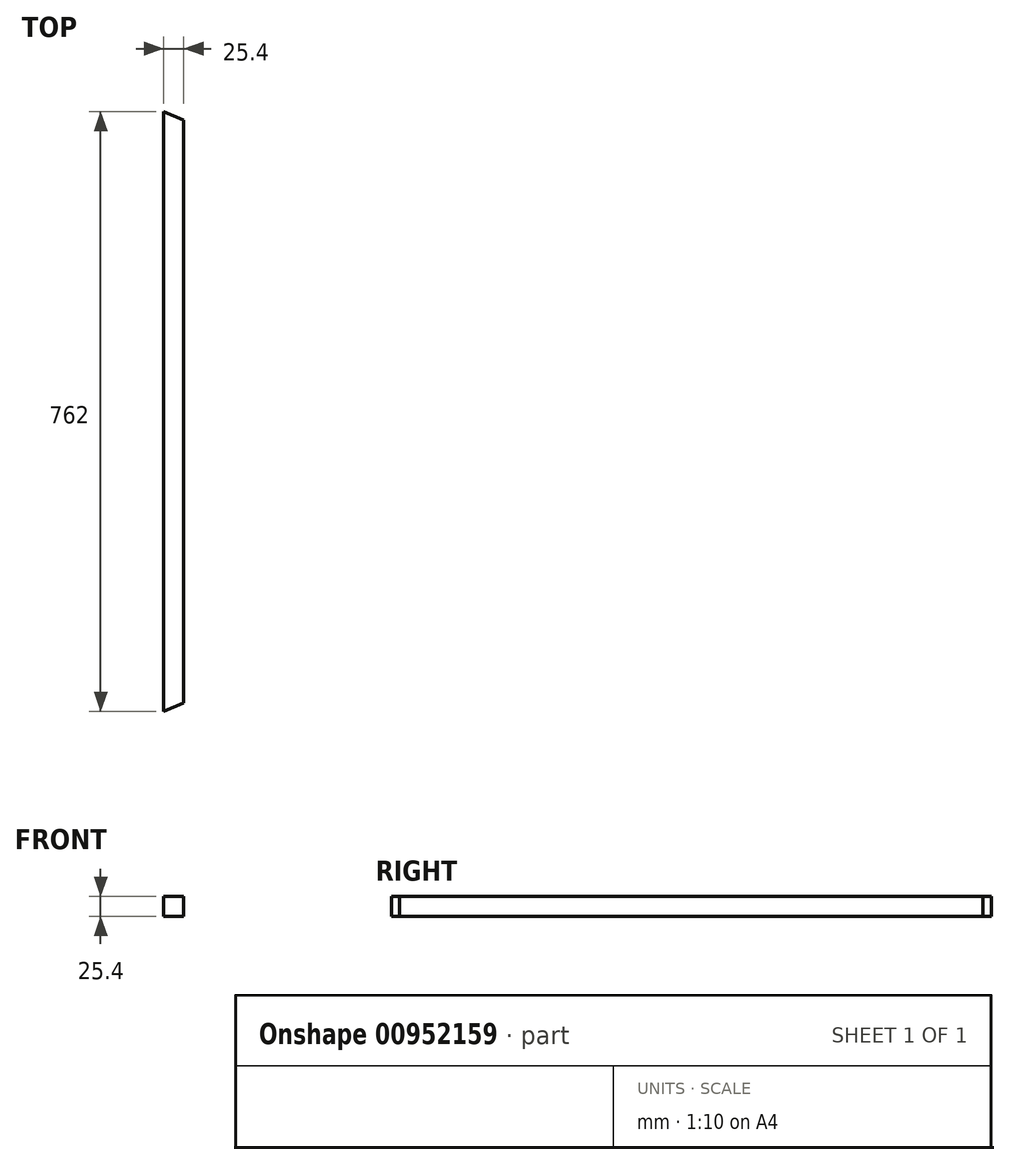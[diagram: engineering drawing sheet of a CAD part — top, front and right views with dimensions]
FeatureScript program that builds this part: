
annotation { "Feature Type Name" : "Feature", "Feature Type Description" : "" }
export const myFeature = defineFeature(function(context is Context, id is Id, definition is map)
    precondition{}
    {
        {
            var Q0;
            Q0=qCreatedBy(makeId("Front.planeOp"),FACE);
            var sketch = newSketch(context, id + "F0", { "sketchPlane" : qUnion([Q0])});
            skLineSegment(sketch, "E0.bottom", {"start": v(12.7, -12.7) * mm, "end": v(-12.7, -12.7) * mm});
            skLineSegment(sketch, "E0.top", {"start": v(12.7, 12.7) * mm, "end": v(-12.7, 12.7) * mm});
            skLineSegment(sketch, "E0.left", {"start": v(12.7, -12.7) * mm, "end": v(12.7, 12.7) * mm});
            skLineSegment(sketch, "E0.right", {"start": v(-12.7, -12.7) * mm, "end": v(-12.7, 12.7) * mm});
            skPoint(sketch, "E0.middle", {"position": v(0, 0) * mm});
            skSolve(sketch);
        }
        {
            var Q0;
            Q0=makeQuery(id+"F0.imprint","IMPRINT",FACE,{"disambiguationData":[TD([[makeQuery(id+"F0.imprint","IMPRINT",EDGE,{"derivedFrom":sQuery(id+"F0.wireOp",EDGE,"E0.bottom")}),-1.0]])]});
            extrude(context, id + "F1", {"entities" : qUnion([Q0]), "endBound" : BoundingType.SYMMETRIC, "depth" : 762 * mm, "offsetDistance" : 25.4 * mm});
        }
        {
            var Q0;
            Q0=makeQuery(id+"F1.opExtrude","CAP_EDGE",EDGE,{"disambiguationData":[OSD([sQuery(id+"F0.wireOp",EDGE,"E0.left")])],"isStart":false});
            var Q1;
            Q1=makeQuery(id+"F1.opExtrude","CAP_EDGE",EDGE,{"disambiguationData":[OSD([sQuery(id+"F0.wireOp",EDGE,"E0.left")])],"isStart":true});
            chamfer(context, id + "F2", {"entities" : qUnion([Q0, Q1]), "chamferType" : ChamferType.OFFSET_ANGLE, "width" : 25.4 * mm, "oppositeDirection" : false, "angle" : 22.5 * degree, "tangentPropagation" : true});
        }
    });
